# Revit family: Hager-Vega_D-IP30-syst-FR-fr
name_source: partatom
category: Electrical Equipment
units: mm (PartAtom-declared; Revit-internal decimal feet)

## family parameters
Cut with Voids When Loaded = No
Host = Face
Panel Configuration = Two Columns, Circuits Across
Part Type = Panelboard
Room Calculation Point = No
Round Connector Dimension = Use Diameter
Shared = No

## types (17) — shared parameters
EF000007 - couleur = EV000202 - blanc
EF000116 - numéro RAL = 9010
EF000118 - avec cadre/support de montage = No
EF001062 - finition CEM = No
EF001088 - possibilité de montage en saillie = Yes
EF001134 - rail DIN = Yes
EF001596 - matériau du boîtier/corps = EV000154 - autre
EF002950 - largeur en nombre de modules = 24
EF005474 - indice de protection (IP) = EV006410 - IP30
EF006244 - couvercle/porte transparent(e) = No
EF006306 - avec serrure = No
EF009212 - finition du couvercle = EV009916 - avec échancrure
EF015777 - borne à conducteur neutre = No
EF015941 - porte pour transmission du signal = No
HG000001 - nombre de colonnes = 1
HG000002 - avec porte = No
HG000003 - Gamme = Vega D
HG000005 - Epaisseur = 3 mm  [stored 0.00984252 ft]
HG000009 - Porte à double battant = No
HG000010 - Portes asymétriques = No
HG000011 - Rangées du bas vides = No
HG000017 - Distance entre pôles = 18 mm  [stored 0.0590551 ft]
Manufacturer = Hager
Type Comments = Vega D
zero-valued in all types: Default Elevation, HG000007 - Nombre de colonnes vides

## per-type parameters (varying)
| type | EF000003 - mode de pose | EF000008 - largeur | EF000040 - hauteur | EF000049 - profondeur | EF000218 - profondeur d'encastrement | EF000266 - nombre de rangées | EF000332 - hauteur d'encastrement | EF000339 - type de capot | EF000846 - largeur d'encastrement | EF001131 - profondeur intérieure | EF015776 - borne de mise à la terre | HG000004 - Référence fabricant | HG000006 - Encastré | HG000008 - Nombre de rangées vides | Model |
| Encastré IP30 L600 H1137 P150 24 Modules - FU62DN | EV000383 - encastré | 600 mm | 1137 mm  [stored 3.73031 ft] | 150 mm | 110 mm  [stored 0.360892 ft] | 6 | 1137 mm  [stored 3.73031 ft] | EV000494 - sans | 600 mm | 110 mm  [stored 0.360892 ft] | No | FU62DN | Yes | 0 | FU62DN |
| Encastré IP30 L600 H1137 P182 24 Modules - FU62AN | EV000383 - encastré | 600 mm | 1137 mm  [stored 3.73031 ft] | 182 mm  [stored 0.597113 ft] | 110 mm  [stored 0.360892 ft] | 4 | 1137 mm  [stored 3.73031 ft] | EV000494 - sans | 600 mm | 110 mm  [stored 0.360892 ft] | No | FU62AN | Yes | 2 | FU62AN |
| Encastré IP30 L600 H1287 P150 24 Modules - FU72DN | EV000383 - encastré | 600 mm | 1287 mm  [stored 4.22244 ft] | 150 mm | 110 mm  [stored 0.360892 ft] | 7 | 1287 mm  [stored 4.22244 ft] | EV000494 - sans | 600 mm | 110 mm  [stored 0.360892 ft] | No | FU72DN | Yes | 0 | FU72DN |
| Encastré IP30 L600 H1287 P182 24 Modules - FU72AN | EV000383 - encastré | 600 mm | 1287 mm  [stored 4.22244 ft] | 182 mm  [stored 0.597113 ft] | 110 mm  [stored 0.360892 ft] | 5 | 1287 mm  [stored 4.22244 ft] | EV000494 - sans | 600 mm | 110 mm  [stored 0.360892 ft] | No | FU72AN | Yes | 2 | FU72AN |
| Encastré IP30 L600 H537 P150 24 Modules - FU22DN | EV000383 - encastré | 600 mm | 537 mm  [stored 1.76181 ft] | 150 mm | 110 mm  [stored 0.360892 ft] | 2 | 537 mm  [stored 1.76181 ft] | EV000494 - sans | 600 mm | 110 mm  [stored 0.360892 ft] | No | FU22DN | Yes | 0 | FU22DN |
| Encastré IP30 L600 H687 P150 24 Modules - FU32DN | EV000383 - encastré | 600 mm | 687 mm  [stored 2.25394 ft] | 150 mm | 110 mm  [stored 0.360892 ft] | 3 | 687 mm  [stored 2.25394 ft] | EV000494 - sans | 600 mm | 110 mm  [stored 0.360892 ft] | No | FU32DN | Yes | 0 | FU32DN |
| Encastré IP30 L600 H687 P182 24 Modules - FU32AN | EV000383 - encastré | 600 mm | 687 mm  [stored 2.25394 ft] | 182 mm  [stored 0.597113 ft] | 110 mm  [stored 0.360892 ft] | 1 | 687 mm  [stored 2.25394 ft] | EV000494 - sans | 600 mm | 110 mm  [stored 0.360892 ft] | No | FU32AN | Yes | 2 | FU32AN |
| Encastré IP30 L600 H837 P150 24 Modules - FU42DN | EV000383 - encastré | 600 mm | 837 mm  [stored 2.74606 ft] | 150 mm | 110 mm  [stored 0.360892 ft] | 4 | 837 mm  [stored 2.74606 ft] | EV000494 - sans | 600 mm | 110 mm  [stored 0.360892 ft] | No | FU42DN | Yes | 0 | FU42DN |
| Encastré IP30 L600 H837 P182 24 Modules - FU42AN | EV000383 - encastré | 600 mm | 837 mm  [stored 2.74606 ft] | 182 mm  [stored 0.597113 ft] | 110 mm  [stored 0.360892 ft] | 2 | 837 mm  [stored 2.74606 ft] | EV000494 - sans | 600 mm | 110 mm  [stored 0.360892 ft] | No | FU42AN | Yes | 2 | FU42AN |
| Encastré IP30 L600 H987 P150 24 Modules - FU52DN | EV000383 - encastré | 600 mm | 987 mm  [stored 3.23819 ft] | 150 mm | 110 mm  [stored 0.360892 ft] | 5 | 987 mm  [stored 3.23819 ft] | EV000494 - sans | 600 mm | 110 mm  [stored 0.360892 ft] | No | FU52DN | Yes | 0 | FU52DN |
| Encastré IP30 L600 H987 P182 24 Modules - FU52AN | EV000383 - encastré | 600 mm | 987 mm  [stored 3.23819 ft] | 182 mm  [stored 0.597113 ft] | 110 mm  [stored 0.360892 ft] | 3 | 987 mm  [stored 3.23819 ft] | EV004216 - porte | 600 mm | 110 mm  [stored 0.360892 ft] | No | FU52AN | Yes | 2 | FU52AN |
| Saillie IP30 L550 H1050 P193 24 Modules - FD62DN | EV000384 - saillie | 550 mm | 1050 mm | 193 mm  [stored 0.633202 ft] | 0 mm  [stored 0 ft] | 6 | 0 mm  [stored 0 ft] | EV000494 - sans | 0 mm  [stored 0 ft] | 189 mm  [stored 0.620079 ft] | Yes | FD62DN | No | 0 | FD62DN |
| Saillie IP30 L550 H1200 P193 24 Modules - FD72DN | EV000384 - saillie | 550 mm | 1200 mm | 193 mm  [stored 0.633202 ft] | 0 mm  [stored 0 ft] | 7 | 0 mm  [stored 0 ft] | EV000494 - sans | 0 mm  [stored 0 ft] | 189 mm  [stored 0.620079 ft] | Yes | FD72DN | No | 0 | FD72DN |
| Saillie IP30 L550 H450 P193 24 Modules - FD22DN | EV000384 - saillie | 550 mm | 450 mm  [stored 1.47638 ft] | 193 mm  [stored 0.633202 ft] | 0 mm  [stored 0 ft] | 2 | 0 mm  [stored 0 ft] | EV000494 - sans | 0 mm  [stored 0 ft] | 193 mm  [stored 0.633202 ft] | Yes | FD22DN | No | 0 | FD22DN |
| Saillie IP30 L550 H600 P193 24 Modules - FD32DN | EV000384 - saillie | 550 mm | 600 mm | 193 mm  [stored 0.633202 ft] | 0 mm  [stored 0 ft] | 3 | 0 mm  [stored 0 ft] | EV000494 - sans | 0 mm  [stored 0 ft] | 193 mm  [stored 0.633202 ft] | Yes | FD32DN | No | 0 | FD32DN |
| Saillie IP30 L550 H750 P193 24 Modules - FD42DN | EV000384 - saillie | 550 mm | 750 mm  [stored 2.46063 ft] | 193 mm  [stored 0.633202 ft] | 0 mm  [stored 0 ft] | 4 | 0 mm  [stored 0 ft] | EV000494 - sans | 0 mm  [stored 0 ft] | 189 mm  [stored 0.620079 ft] | Yes | FD42DN | No | 0 | FD42DN |
| Saillie IP30 L550 H900 P193 24 Modules - FD52DN | EV000384 - saillie | 550 mm | 900 mm  [stored 2.95276 ft] | 193 mm  [stored 0.633202 ft] | 0 mm  [stored 0 ft] | 5 | 0 mm  [stored 0 ft] | EV000494 - sans | 0 mm  [stored 0 ft] | 189 mm  [stored 0.620079 ft] | Yes | FD52DN | No | 0 | FD52DN |

note: [stored X ft] marks values corroborated as IEEE doubles in the binary element streams (Revit-internal decimal feet)

## geometry (parser evidence)
native form markers: Sweep x17
no freeform markers — native parametric forms only
